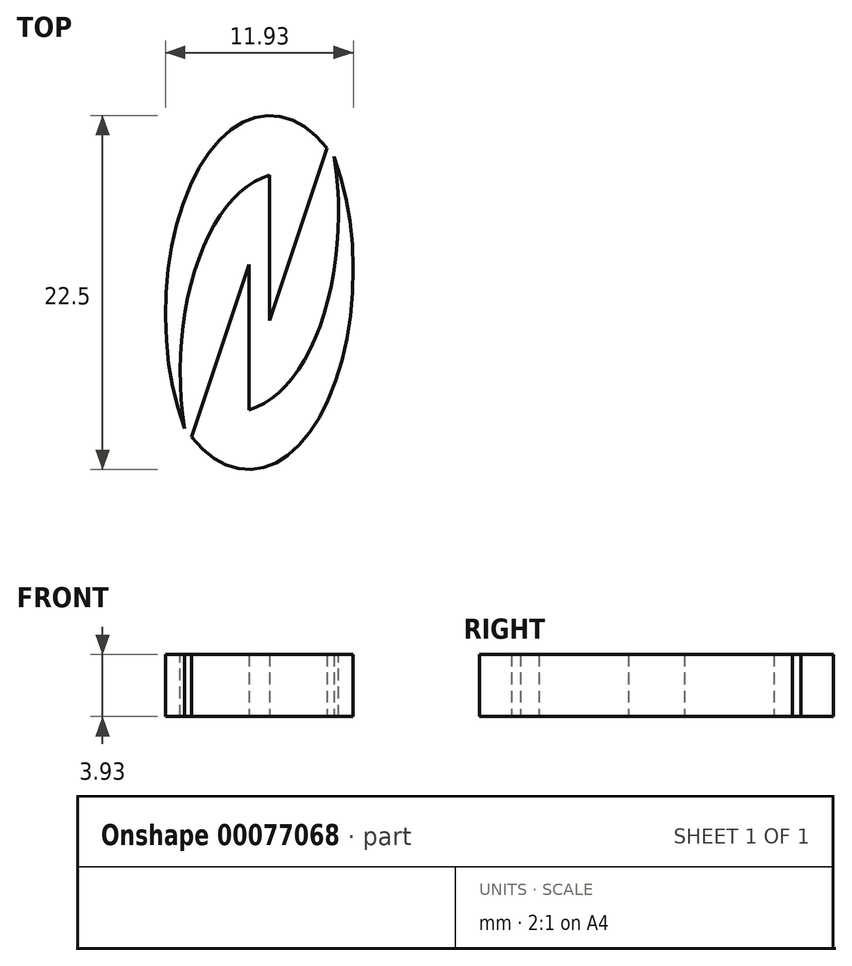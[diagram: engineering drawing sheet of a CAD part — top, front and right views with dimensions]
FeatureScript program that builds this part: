
annotation { "Feature Type Name" : "Feature", "Feature Type Description" : "" }
export const myFeature = defineFeature(function(context is Context, id is Id, definition is map)
    precondition{}
    {
        {
            var Q0;
            Q0=qCreatedBy(makeId("Top.planeOp"),FACE);
            var sketch = newSketch(context, id + "F0", { "sketchPlane" : qUnion([Q0])});
            skEllipticalArc(sketch, "E0", {});
            skLineSegment(sketch, "E1", {"start": v(0, 0) * mm, "end": v(4.1, 0) * mm});
            skLineSegment(sketch, "E2", {"start": v(4.88, -1.61) * mm, "end": v(0, 0) * mm});
            skEllipticalArc(sketch, "E3", {});
            skPoint(sketch, "E4.orphan", {"position": v(-5.41, 0) * mm});
            skPoint(sketch, "E5.orphan", {"position": v(5.8, 0) * mm});
            skEllipticalArc(sketch, "E6", {});
            skLineSegment(sketch, "E7", {"start": v(1.6, 0.59) * mm, "end": v(-2.51, 0.59) * mm});
            skLineSegment(sketch, "E8", {"start": v(-3.29, 2.2) * mm, "end": v(1.6, 0.59) * mm});
            skEllipticalArc(sketch, "E9", {});
            skPoint(sketch, "E10.orphan", {"position": v(-4.2, 0.59) * mm});
            const initialGuessF0  = {"E0": [0.00019164077152911984, 0, 1, 0, 0.005605491204728483, 0.0029456090684606678, 5.702943639447654, 2.1851302894137667], "E3": [-0.0014400467494755573, -0.0004161340610454776, 1, 0, 0.005605491204728483, 0.0029456090684606678, 0.14174686152028323, 1.8601439761282659], "E6": [0.0014026231809860835, 0.0005895231286726097, -1, 0, 0.005605491204728483, 0.0029456090684606678, 5.702943639447654, 2.1851302894137667], "E9": [0.003034310701990761, 0.0010056571897180866, -1, 0, 0.005605491204728483, 0.0029456090684606678, 0.14174686152028318, 1.8601439761282659]};
            skSetInitialGuess(sketch, initialGuessF0);
            skSolve(sketch);
        }
        {
            var Q0;
            Q0=makeQuery(id+"F0.imprint","IMPRINT",FACE,{"disambiguationData":[TD([[makeQuery(id+"F0.imprint","IMPRINT",EDGE,{"derivedFrom":sQuery(id+"F0.wireOp",EDGE,"E6")}),1.0]])]});
            var Q1;
            Q1=makeQuery(id+"F0.imprint","IMPRINT",FACE,{"disambiguationData":[TD([[makeQuery(id+"F0.imprint","IMPRINT",EDGE,{"derivedFrom":sQuery(id+"F0.wireOp",EDGE,"E0")}),1.0]])]});
            extrude(context, id + "F1", {"entities" : qUnion([Q0, Q1]), "depth" : 1.75 * mm, "offsetDistance" : 25 * mm});
        }
        {
            var Q0;
            Q0=qCreatedBy(makeId("Front.planeOp"),FACE);
            var sketch = newSketch(context, id + "F2", { "sketchPlane" : qUnion([Q0])});
            skLineSegment(sketch, "E11", {"start": v(0, 24) * mm, "end": v(0, -22.36) * mm});
            skSolve(sketch);
        }
        {
            var Q0;
            Q0=makeQuery(id+"F1.opExtrude","SWEPT_BODY",BODY,{"disambiguationData":[OSD([sQuery(id+"F0.wireOp",EDGE,"E6"),sQuery(id+"F0.wireOp",EDGE,"E7"),sQuery(id+"F0.wireOp",EDGE,"E8"),sQuery(id+"F0.wireOp",EDGE,"E9")])]});
            var Q1;
            Q1=makeQuery(id+"F1.opExtrude","SWEPT_BODY",BODY,{"disambiguationData":[OSD([sQuery(id+"F0.wireOp",EDGE,"E0"),sQuery(id+"F0.wireOp",EDGE,"E1"),sQuery(id+"F0.wireOp",EDGE,"E2"),sQuery(id+"F0.wireOp",EDGE,"E3")])]});
            var Q2;
            Q2=sQuery(id+"F2.wireOp",EDGE,"E11");
            transform(context, id + "F3", {"entities" : qUnion([Q0, Q1]), "transformType" : TransformType.ROTATION, "transformAxis" : qUnion([Q2]), "angle" : 90 * degree, "makeCopy" : false});
        }
        {
            var Q0;
            Q0=makeQuery(id+"F1.opExtrude","SWEPT_BODY",BODY,{"disambiguationData":[OSD([sQuery(id+"F0.wireOp",EDGE,"E0"),sQuery(id+"F0.wireOp",EDGE,"E1"),sQuery(id+"F0.wireOp",EDGE,"E2"),sQuery(id+"F0.wireOp",EDGE,"E3")])]});
            var Q1;
            Q1=makeQuery(id+"F1.opExtrude","SWEPT_BODY",BODY,{"disambiguationData":[OSD([sQuery(id+"F0.wireOp",EDGE,"E6"),sQuery(id+"F0.wireOp",EDGE,"E7"),sQuery(id+"F0.wireOp",EDGE,"E8"),sQuery(id+"F0.wireOp",EDGE,"E9")])]});
            var Q2;
            Q2=makeQuery(id+"F1.opExtrude","CAP_VERTEX",VERTEX,{"disambiguationData":[OSD([sQuery(id+"F0.wireOp",EDGE,"E7"),sQuery(id+"F0.wireOp",EDGE,"E8")])],"isStart":false});
            transform(context, id + "F4", {"entities" : qUnion([Q0, Q1]), "transformType" : TransformType.SCALE_UNIFORMLY, "scale" : 1.5, "scalePoint" : qUnion([Q2]), "makeCopy" : false});
        }
        {
            var Q0;
            Q0=makeQuery(id+"F1.opExtrude","SWEPT_BODY",BODY,{"disambiguationData":[OSD([sQuery(id+"F0.wireOp",EDGE,"E6"),sQuery(id+"F0.wireOp",EDGE,"E7"),sQuery(id+"F0.wireOp",EDGE,"E8"),sQuery(id+"F0.wireOp",EDGE,"E9")])]});
            var Q1;
            Q1=makeQuery(id+"F1.opExtrude","SWEPT_BODY",BODY,{"disambiguationData":[OSD([sQuery(id+"F0.wireOp",EDGE,"E0"),sQuery(id+"F0.wireOp",EDGE,"E1"),sQuery(id+"F0.wireOp",EDGE,"E2"),sQuery(id+"F0.wireOp",EDGE,"E3")])]});
            var Q2;
            Q2=qCreatedBy(makeId("Origin.pointOp"),VERTEX);
            transform(context, id + "F5", {"entities" : qUnion([Q0, Q1]), "transformType" : TransformType.SCALE_UNIFORMLY, "scale" : 1.5, "scalePoint" : qUnion([Q2]), "makeCopy" : false});
        }
    });
